# Revit family: PRD_AR_JntrlUnits_SiriusMultiPurposeSink_BS313N,314N,CA210-2N,7N
name_source: partatom
category: Plumbing Fixtures
revit_build: Autodesk Revit 2018 (Build: 20190510_1515(x64)
units: mm (PartAtom-declared; Revit-internal decimal feet)

## family parameters
Cut with Voids When Loaded = No
Host = Face
OmniClass Number = 23.45.05.14.14
OmniClass Title = Sinks/Lavatories
Part Type = Normal
Room Calculation Point = No
Round Connector Dimension = Use Diameter
Shared = No

## types (4) — shared parameters
AssetType = Fixed
Category = Pr_40_20_96_44, Janitorial sinks
Default Elevation = 850 mm  [stored 2.78871 ft]
DrainSize = DN 40 (1 1/2 inch.)
DurationUnit = year
Form = Stainless steel multi purpose sink
GrossWeight = 9.90 kg
IfcExportAs = IfcSanitaryTerminalType
IfcExportType = SINK
IntegralAccessories = incl. stainless steel screws and dowels
Manufacturer = KWC Group AG
ManufacturerName = KWC Group AG
ManufacturerURL = www.kwc.com
Material = Stainless steel
NBSDescription = Janitorial units
NBSReference = 45-35-70/401
NetWeight = 8.90 kg
NominalDepth = 500 mm  [stored 1.64042 ft]
NominalHeight = 354 mm  [stored 1.16142 ft]
NominalWidth = 750 mm  [stored 2.46063 ft]
OutletSize = DN 40 (1 1/2 inch.)
ProductInformation = https://pim.kwc.com
Shape = Rectangular
SinkMaterial = PRD_AR_StainlessSteel_SatinFinished
SinkMounting = WallHung
SinkType = Other
Size = 750 x 500 x 354 mm
URL = www.kwc.com
Uniclass2015Code = Pr_40_20_96_44
Uniclass2015Title = Janitorial sinks
Uniclass2015Version = Products v1.10
Version = 1
WarrantyDurationUnit = year
WasteSize = 40  [stored 0.131234 ft]
WaterSupplyOverflowAndWasteHolesOverflow = Stand pipe overflow
WaterSupplyOverflowAndWasteHolesWaterSupply = No tapholes

## per-type parameters (varying)
| type | BIMObjectName | BS313N | BS314N | Color | Description | Features | Finish | FinishAndMaterial | ModelNumber | Name | WaterSupplyOverflowAndWasteHolesWaste |
| BS313N | PRD_AR_JanitorialUnits_SiriusMultiPurposeSink_BS313N | Yes | No | Stainless steel | SIRIUS washtrough for wall mounting, stainless steel, satin finished surface, material thickness of trough 0.8 mm / side panels 1.2mm, side panels with integrated wall brackets, seamlessly welded, front panel with rubbing board, 70 mm lowered tap ledge, no overflow, 40 mm rear upstand, left hand waste, G 1 1/2 B plastic standpipe strainer, removable corner protection plate, includes
fixings. | stainless steel, 0.80 mm, satin finished, wall mounting, 750x354x500 mm (WxHxD) | Satin finished | Stainless steel 1.4301 | 2030045753 | Sirius multi purpose sink BS313N | Left-Back-Corner |
| BS314N | PRD_AR_JanitorialUnits_SiriusMultiPurposeSink_BS314N | No | Yes | Stainless steel | SIRIUS washtrough for wall mounting, stainless steel, satin finished surface, material thickness of trough 0.8 mm / side panels 1.2 mm, side panels with integrated wall brackets, seamlessly welded, front panel with rubbing board, 70 mm lowered tap landing, no overflow, 40 mm rear upstand, right hand waste, G 1 1/2 B plastic standpipe strainer, removable corner protection plate, includes fixings. | stainless steel, 0.80 mm, satin finished, wall mounting, 750x354x500 mm (WxHxD) | Satin finished | Stainless steel 1.4301 | 2030045754 | Sirius multi purpose sink BS314N | Right-Back-Corner |
| CA210-2N | PRD_AR_JanitorialUnits_SiriusMultiPurposeSink_CA210-2N | Yes | No |  | SIRIUS washtrough for wall mounting, chromium steel, surface high polished, material thickness of trough 0.8 mm / side panels 1.2 mm, side panels with integrated wall brackets, seamlessly welded, front panel with rubbing board, 70 mm lowered tap landing, no overflow, 40 mm rear upstand, right hand drain, G 1 1/2 B plastic standpipe strainer, removable corner protection plate, fixings included. | chromium steel, 0.80 mm, high polished, wall mounting, 750x354x500 mm (WxHxD) | High polished | Chromium steel 1.4016 | 2030045758 | Sirius multi purpose sink CA210-2N | Right-Back-Corner |
| CA210-7N | PRD_AR_JanitorialUnits_SiriusMultiPurposeSink_CA210-7N | No | Yes |  | SIRIUS washtrough for wall mounting, chromium steel, surface high polished, material thickness of trough 0.8 mm / side panels 1.2 mm, side panels with integrated wall brackets, seamlessly welded, front panel with rubbing board, 70 mm lowered tap landing, no overflow, 40 mm rear upstand, left hand drain, G 1 1/2 B plastic standpipe strainer, removable corner protection plate, fixings included. | chromium steel, 0.80 mm, high polished, wall mounting, 750x354x500 mm (WxHxD) | High polished | Chromium steel 1.4016 | 2030045759 | Sirius multi purpose sink CA210-7N | Left-Back-Corner |

note: column(s) folded — value = type name in every type: Model, ModelReference

note: [stored X ft] marks values corroborated as IEEE doubles in the binary element streams (Revit-internal decimal feet)

## geometry (parser evidence)
native form markers: Sweep x10
no freeform markers — native parametric forms only
